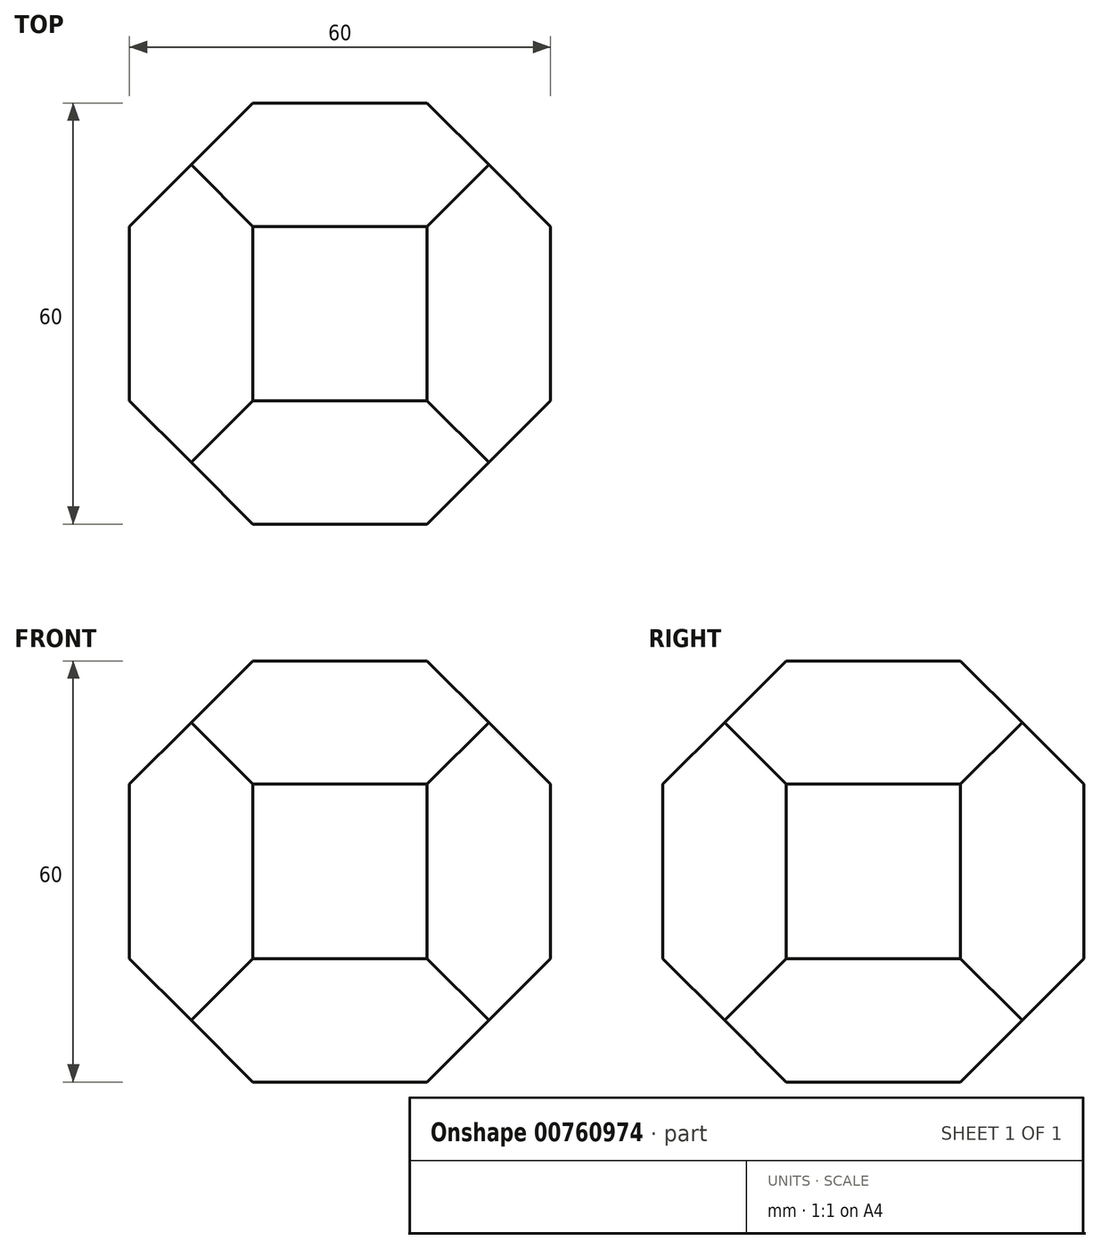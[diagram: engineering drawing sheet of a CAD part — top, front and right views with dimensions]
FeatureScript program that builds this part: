
annotation { "Feature Type Name" : "Feature", "Feature Type Description" : "" }
export const myFeature = defineFeature(function(context is Context, id is Id, definition is map)
    precondition{}
    {
        {
            var Q0;
            Q0=qCreatedBy(makeId("Front.planeOp"),FACE);
            var sketch = newSketch(context, id + "F0", { "sketchPlane" : qUnion([Q0])});
            skCircle(sketch, "E0.cCircle", {"center": v(0, 0) * mm, "radius": 30 * mm, "construction": true});
            skLineSegment(sketch, "E0.0", {"start": v(-30, -12.43) * mm, "end": v(-30, 12.43) * mm});
            skLineSegment(sketch, "E0.1", {"start": v(-30, 12.43) * mm, "end": v(-12.43, 30) * mm});
            skLineSegment(sketch, "E0.2", {"start": v(-12.43, 30) * mm, "end": v(12.43, 30) * mm});
            skLineSegment(sketch, "E0.3", {"start": v(12.43, 30) * mm, "end": v(30, 12.43) * mm});
            skLineSegment(sketch, "E0.4", {"start": v(30, 12.43) * mm, "end": v(30, -12.43) * mm});
            skLineSegment(sketch, "E0.5", {"start": v(30, -12.43) * mm, "end": v(12.43, -30) * mm});
            skLineSegment(sketch, "E0.6", {"start": v(12.43, -30) * mm, "end": v(-12.43, -30) * mm});
            skLineSegment(sketch, "E0.7", {"start": v(-12.43, -30) * mm, "end": v(-30, -12.43) * mm});
            skPoint(sketch, "E0.0.midPoint", {"position": v(-30, 0) * mm});
            skSolve(sketch);
        }
        {
            var Q0;
            Q0=qCreatedBy(makeId("Top.planeOp"),FACE);
            var sketch = newSketch(context, id + "F1", { "sketchPlane" : qUnion([Q0])});
            skCircle(sketch, "E1.cCircle", {"center": v(0, 0) * mm, "radius": 30 * mm, "construction": true});
            skLineSegment(sketch, "E1.0", {"start": v(30, 12.43) * mm, "end": v(30, -12.43) * mm});
            skLineSegment(sketch, "E1.1", {"start": v(30, -12.43) * mm, "end": v(12.43, -30) * mm});
            skLineSegment(sketch, "E1.2", {"start": v(12.43, -30) * mm, "end": v(-12.43, -30) * mm});
            skLineSegment(sketch, "E1.3", {"start": v(-12.43, -30) * mm, "end": v(-30, -12.43) * mm});
            skLineSegment(sketch, "E1.4", {"start": v(-30, -12.43) * mm, "end": v(-30, 12.43) * mm});
            skLineSegment(sketch, "E1.5", {"start": v(-30, 12.43) * mm, "end": v(-12.43, 30) * mm});
            skLineSegment(sketch, "E1.6", {"start": v(-12.43, 30) * mm, "end": v(12.43, 30) * mm});
            skLineSegment(sketch, "E1.7", {"start": v(12.43, 30) * mm, "end": v(30, 12.43) * mm});
            skPoint(sketch, "E1.0.midPoint", {"position": v(30, 0) * mm});
            skSolve(sketch);
        }
        {
            var Q0;
            Q0=qCreatedBy(makeId("Right.planeOp"),FACE);
            var sketch = newSketch(context, id + "F2", { "sketchPlane" : qUnion([Q0])});
            skCircle(sketch, "E2.cCircle", {"center": v(0, 0) * mm, "radius": 30 * mm, "construction": true});
            skLineSegment(sketch, "E2.0", {"start": v(-12.43, 30) * mm, "end": v(12.43, 30) * mm});
            skLineSegment(sketch, "E2.1", {"start": v(12.43, 30) * mm, "end": v(30, 12.43) * mm});
            skLineSegment(sketch, "E2.2", {"start": v(30, 12.43) * mm, "end": v(30, -12.43) * mm});
            skLineSegment(sketch, "E2.3", {"start": v(30, -12.43) * mm, "end": v(12.43, -30) * mm});
            skLineSegment(sketch, "E2.4", {"start": v(12.43, -30) * mm, "end": v(-12.43, -30) * mm});
            skLineSegment(sketch, "E2.5", {"start": v(-12.43, -30) * mm, "end": v(-30, -12.43) * mm});
            skLineSegment(sketch, "E2.6", {"start": v(-30, -12.43) * mm, "end": v(-30, 12.43) * mm});
            skLineSegment(sketch, "E2.7", {"start": v(-30, 12.43) * mm, "end": v(-12.43, 30) * mm});
            skPoint(sketch, "E2.0.midPoint", {"position": v(0, 30) * mm});
            skSolve(sketch);
        }
        {
            var Q0;
            Q0=qSketchRegion(id+"F0",true);
            extrude(context, id + "F3", {"entities" : qUnion([Q0]), "endBound" : BoundingType.SYMMETRIC, "depth" : 60 * mm});
        }
        {
            var Q0;
            Q0=qSketchRegion(id+"F1",true);
            extrude(context, id + "F4", {"entities" : qUnion([Q0]), "operationType" : NewBodyOperationType.INTERSECT, "endBound" : BoundingType.SYMMETRIC, "depth" : 60 * mm});
        }
        {
            var Q0;
            Q0=qSketchRegion(id+"F2",true);
            extrude(context, id + "F5", {"entities" : qUnion([Q0]), "operationType" : NewBodyOperationType.INTERSECT, "endBound" : BoundingType.SYMMETRIC, "depth" : 60 * mm});
        }
    });
